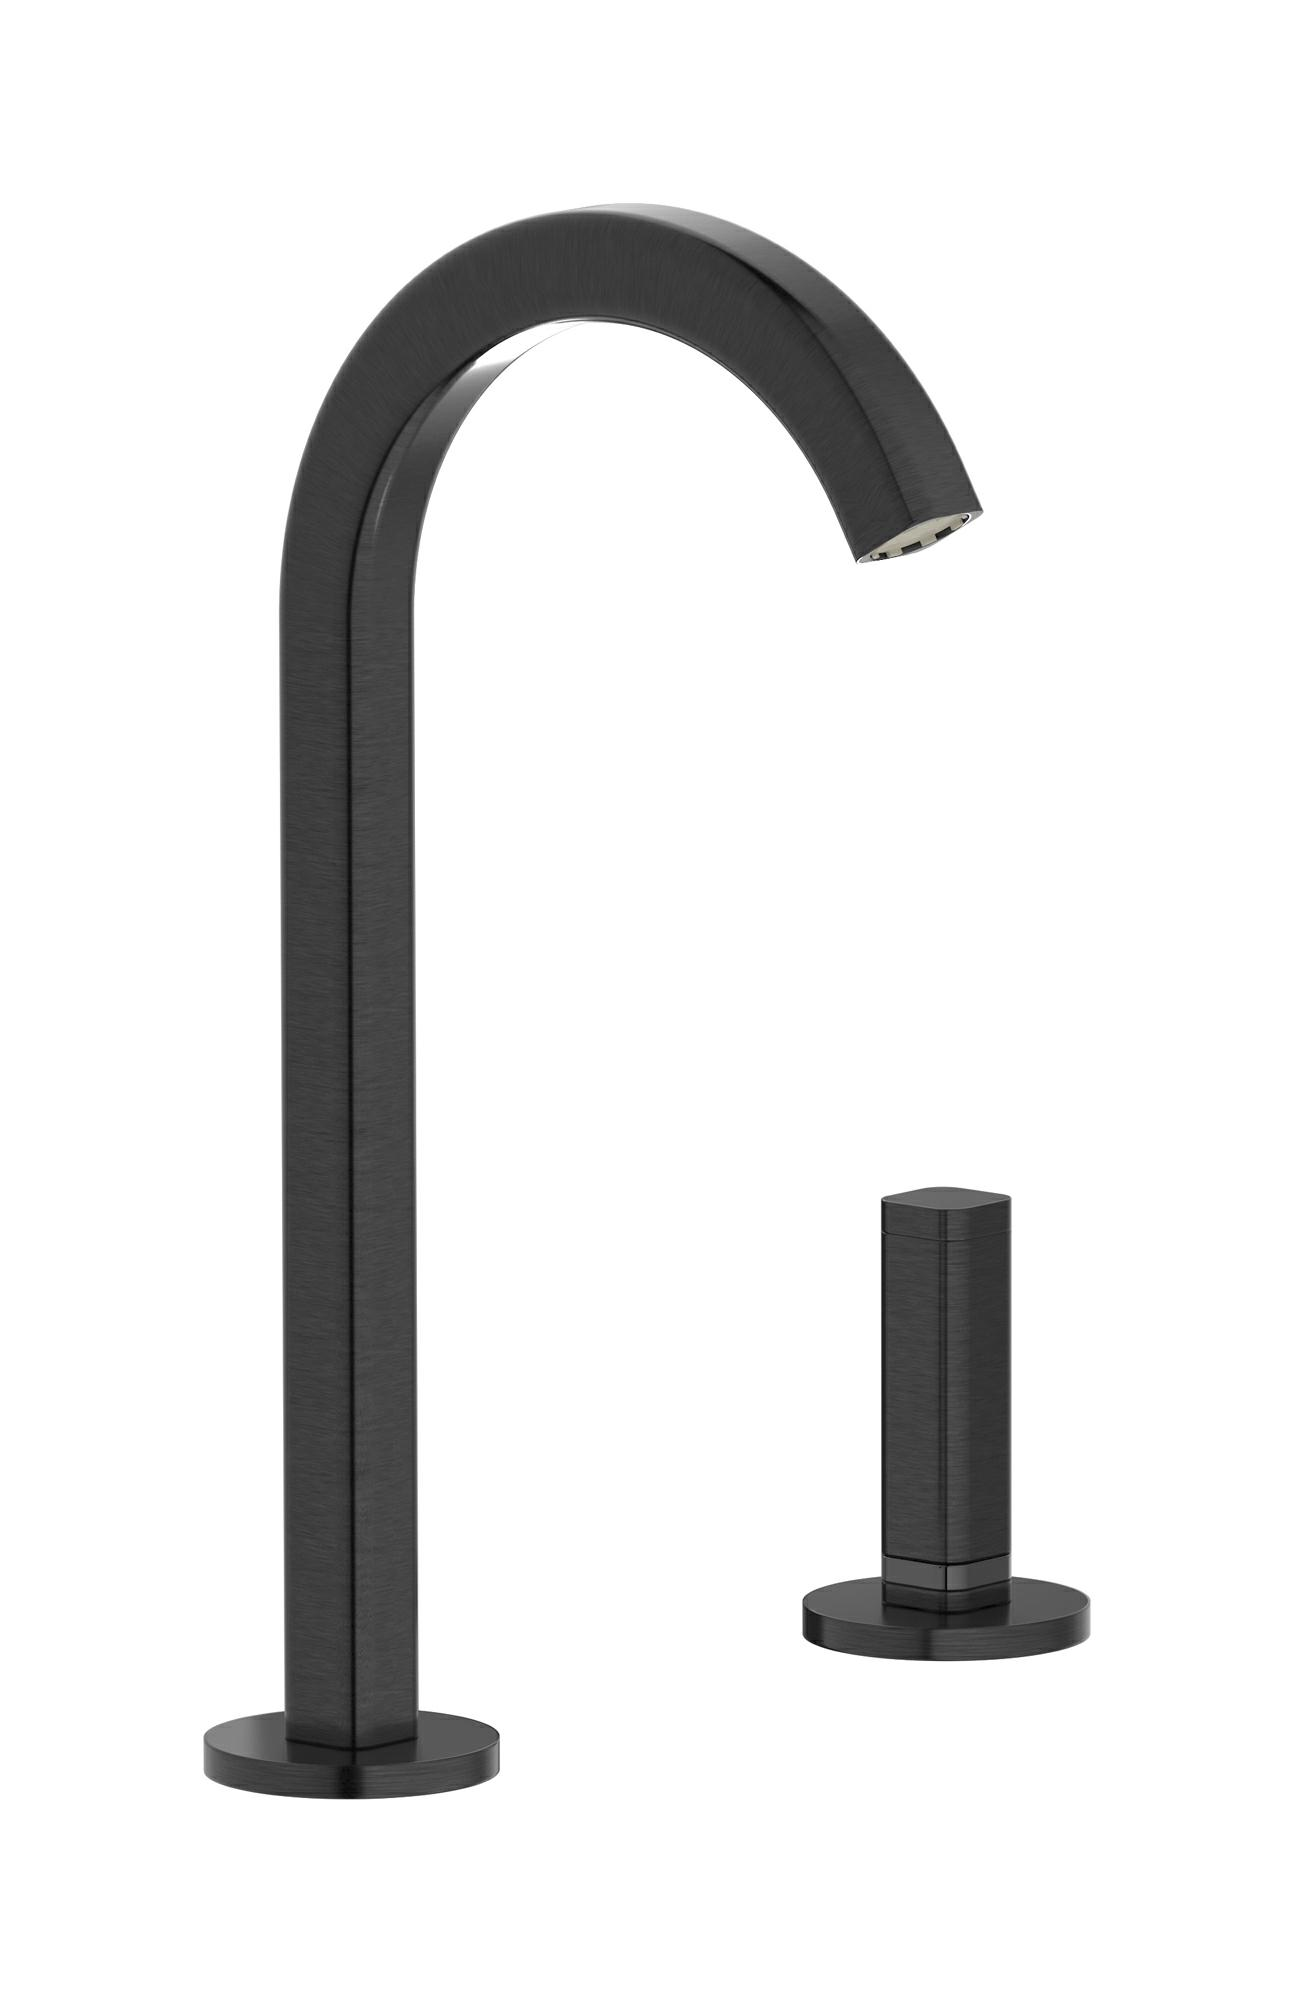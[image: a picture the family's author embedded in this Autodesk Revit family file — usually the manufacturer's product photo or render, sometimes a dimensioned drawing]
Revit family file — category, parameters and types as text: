
# Revit family: EI394_1
name_source: partatom
category: Apparecchi idraulici
units: mm (PartAtom-declared; Revit-internal decimal feet)

## family parameters
Basato su piano di lavoro = No
Condiviso = No
Mantieni orientamento annotazione = No
Numero OmniClass = 23.45.55.17
Punto di calcolo locali = No
Quota connettore circolare = Usa diametro
Sempre verticale = Sì
Taglio con vuoti quando caricato = No
Tipo di parte = Normale
Titolo OmniClass = Mixing Faucets

## types (12) — shared parameters
Cold water inlet = 10 mm  [stored 0.0328084 ft]
Commenti sul tipo = Washbasin
Connessione CW = No
Connessione HW = No
Connessione di scarico = No
Connessione di ventilazione = No
Descrizione = Washbasin two hole mixer
Hot water inlet = 10 mm  [stored 0.0328084 ft]
Produttore = IB Rubinetterie S.p.A.
URL = https://www.weareib.it
zero-valued in all types: Prospetto di default

## per-type parameters (varying)
| type | Finishes surface | Immagine tipo | Modello |
| Chrome | IB_Chrome | EI394CC_1.jpg | EI394CC_1 |
| Brushed nickel | IB_Brushed nickel | EI394SS_1.jpg | EI394SS_1 |
| Matt black | IB_matt black | EI394NP_1.jpg | EI394NP_1 |
| Natural brass | IB_Brass | EI394ON_1.jpg | EI394ON_1 |
| Black chrome | IB_Black chrome | EI394CF_1.jpg | EI394CF_1 |
| Brushed black chrome | IB_Brushed black chrome | EI394CS_1.jpg | EI394CS_1 |
| Pale gold | IB_Pale gold | EI394II_1.jpg | EI394II_1 |
| Brushed pale gold | IB_Pale gold | EI394IS_1.jpg | EI394IS_1 |
| Rose gold | IB_Rose gold | EI394RS_1.jpg | EI394RS_1 |
| Brushed gold | IB_brushed gold | EI394OS_1.jpg | EI394OS_1 |
| Brushed rose gold | IB_Brushed rose gold | EI394SR_1.jpg | EI394SR_1 |
| Gold | IB_gold | EI394OO_1.jpg | EI394OO_1 |

note: [stored X ft] marks values corroborated as IEEE doubles in the binary element streams (Revit-internal decimal feet)
